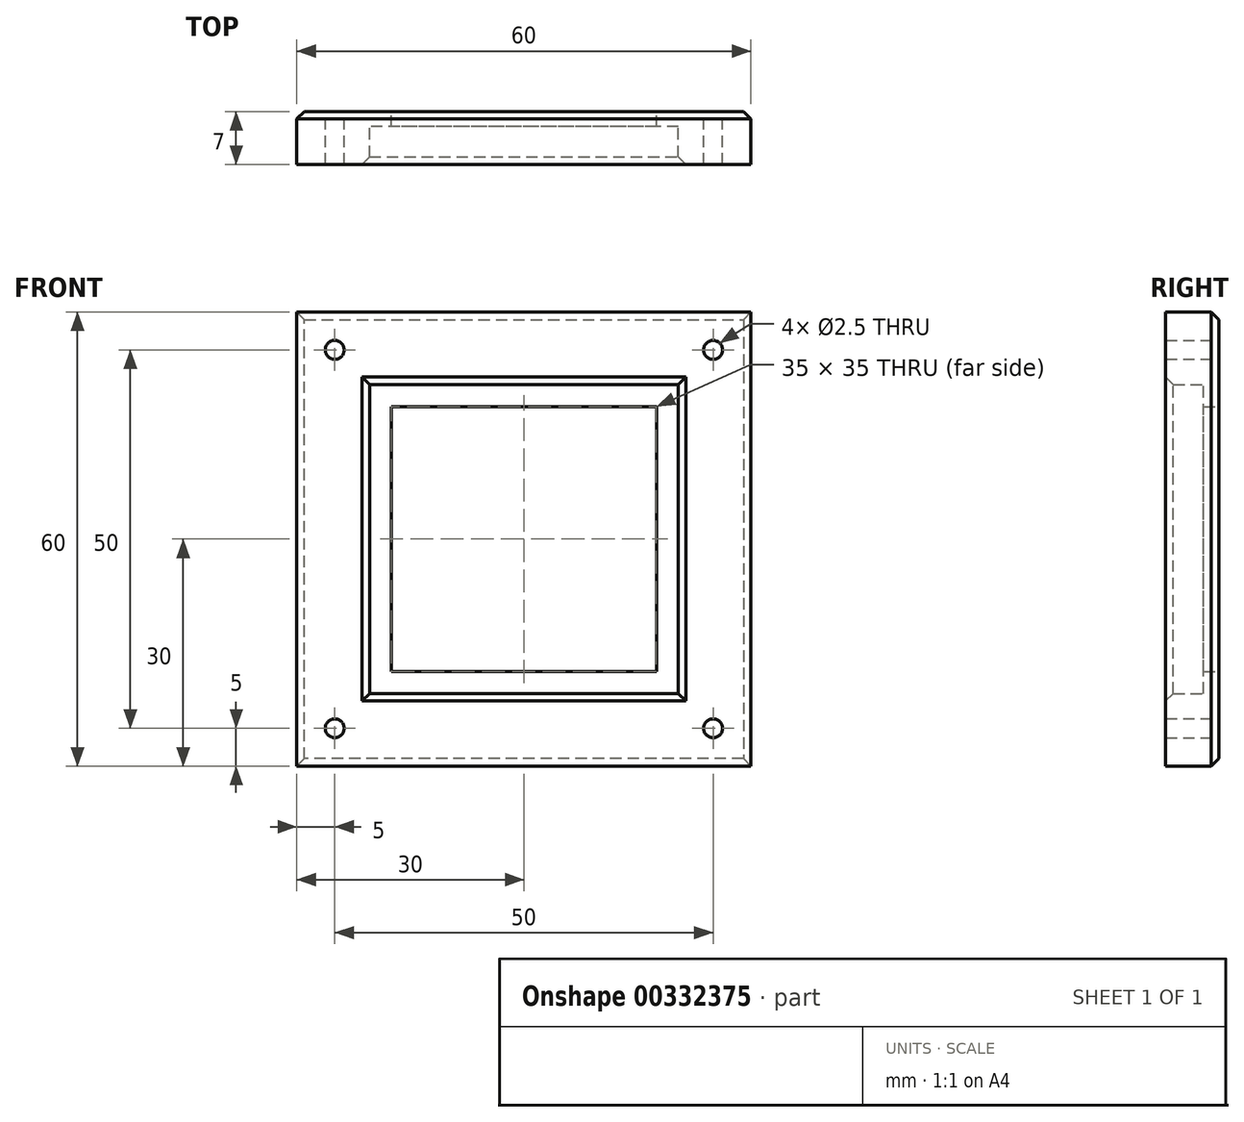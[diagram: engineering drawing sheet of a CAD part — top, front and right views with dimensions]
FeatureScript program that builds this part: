
annotation { "Feature Type Name" : "Feature", "Feature Type Description" : "" }
export const myFeature = defineFeature(function(context is Context, id is Id, definition is map)
    precondition{}
    {
        {
            var Q0;
            Q0=qCreatedBy(makeId("Front.planeOp"),FACE);
            var sketch = newSketch(context, id + "F0", { "sketchPlane" : qUnion([Q0])});
            skLineSegment(sketch, "E0.bottom", {"start": v(30, -30) * mm, "end": v(-30, -30) * mm});
            skLineSegment(sketch, "E0.top", {"start": v(30, 30) * mm, "end": v(-30, 30) * mm});
            skLineSegment(sketch, "E0.left", {"start": v(30, -30) * mm, "end": v(30, 30) * mm});
            skLineSegment(sketch, "E0.right", {"start": v(-30, -30) * mm, "end": v(-30, 30) * mm});
            skPoint(sketch, "E0.middle", {"position": v(0, 0) * mm});
            skLineSegment(sketch, "E1.bottom", {"start": v(17.5, -17.5) * mm, "end": v(-17.5, -17.5) * mm});
            skLineSegment(sketch, "E1.top", {"start": v(17.5, 17.5) * mm, "end": v(-17.5, 17.5) * mm});
            skLineSegment(sketch, "E1.left", {"start": v(17.5, -17.5) * mm, "end": v(17.5, 17.5) * mm});
            skLineSegment(sketch, "E1.right", {"start": v(-17.5, -17.5) * mm, "end": v(-17.5, 17.5) * mm});
            skCircle(sketch, "E2", {"center": v(-25, 25) * mm, "radius": 1.25 * mm});
            skCircle(sketch, "E3", {"center": v(-25, -25) * mm, "radius": 1.25 * mm});
            skCircle(sketch, "E4", {"center": v(25, 25) * mm, "radius": 1.25 * mm});
            skCircle(sketch, "E5", {"center": v(25, -25) * mm, "radius": 1.25 * mm});
            skLineSegment(sketch, "E6.bottom", {"start": v(20.4, -20.4) * mm, "end": v(-20.4, -20.4) * mm});
            skLineSegment(sketch, "E6.top", {"start": v(20.4, 20.4) * mm, "end": v(-20.4, 20.4) * mm});
            skLineSegment(sketch, "E6.left", {"start": v(20.4, -20.4) * mm, "end": v(20.4, 20.4) * mm});
            skLineSegment(sketch, "E6.right", {"start": v(-20.4, -20.4) * mm, "end": v(-20.4, 20.4) * mm});
            skSolve(sketch);
        }
        {
            var Q0;
            Q0=makeQuery(id+"F0.imprint","IMPRINT",FACE,{"disambiguationData":[TD([[makeQuery(id+"F0.imprint","IMPRINT",EDGE,{"derivedFrom":sQuery(id+"F0.wireOp",EDGE,"E0.bottom")}),-1.0]])]});
            extrude(context, id + "F1", {"entities" : qUnion([Q0]), "depth" : 7 * mm});
        }
        {
            var Q0;
            Q0=makeQuery(id+"F0.imprint","IMPRINT",FACE,{"disambiguationData":[TD([[makeQuery(id+"F0.imprint","IMPRINT",EDGE,{"derivedFrom":sQuery(id+"F0.wireOp",EDGE,"E1.bottom")}),1.0]])]});
            extrude(context, id + "F2", {"entities" : qUnion([Q0]), "operationType" : NewBodyOperationType.ADD, "depth" : 2 * mm});
        }
        {
            var Q0;
            Q0=makeQuery(id+"F1.opExtrude","CAP_EDGE",EDGE,{"disambiguationData":[OSD([sQuery(id+"F0.wireOp",EDGE,"E6.left")])],"isStart":false});
            var Q1;
            Q1=makeQuery(id+"F1.opExtrude","CAP_EDGE",EDGE,{"disambiguationData":[OSD([sQuery(id+"F0.wireOp",EDGE,"E6.top")])],"isStart":false});
            var Q2;
            Q2=makeQuery(id+"F1.opExtrude","CAP_EDGE",EDGE,{"disambiguationData":[OSD([sQuery(id+"F0.wireOp",EDGE,"E6.right")])],"isStart":false});
            var Q3;
            Q3=makeQuery(id+"F1.opExtrude","CAP_EDGE",EDGE,{"disambiguationData":[OSD([sQuery(id+"F0.wireOp",EDGE,"E6.bottom")])],"isStart":false});
            chamfer(context, id + "F3", {"entities" : qUnion([Q0, Q1, Q2, Q3]), "width" : 1 * mm, "tangentPropagation" : true});
        }
        {
            var Q0;
            Q0=makeQuery(id+"F1.opExtrude","CAP_EDGE",EDGE,{"disambiguationData":[OSD([sQuery(id+"F0.wireOp",EDGE,"E0.right")])],"isStart":true});
            var Q1;
            Q1=makeQuery(id+"F1.opExtrude","CAP_EDGE",EDGE,{"disambiguationData":[OSD([sQuery(id+"F0.wireOp",EDGE,"E0.bottom")])],"isStart":true});
            var Q2;
            Q2=makeQuery(id+"F1.opExtrude","CAP_EDGE",EDGE,{"disambiguationData":[OSD([sQuery(id+"F0.wireOp",EDGE,"E0.left")])],"isStart":true});
            var Q3;
            Q3=makeQuery(id+"F1.opExtrude","CAP_EDGE",EDGE,{"disambiguationData":[OSD([sQuery(id+"F0.wireOp",EDGE,"E0.top")])],"isStart":true});
            chamfer(context, id + "F4", {"entities" : qUnion([Q0, Q1, Q2, Q3]), "width" : 1 * mm, "tangentPropagation" : true});
        }
    });
